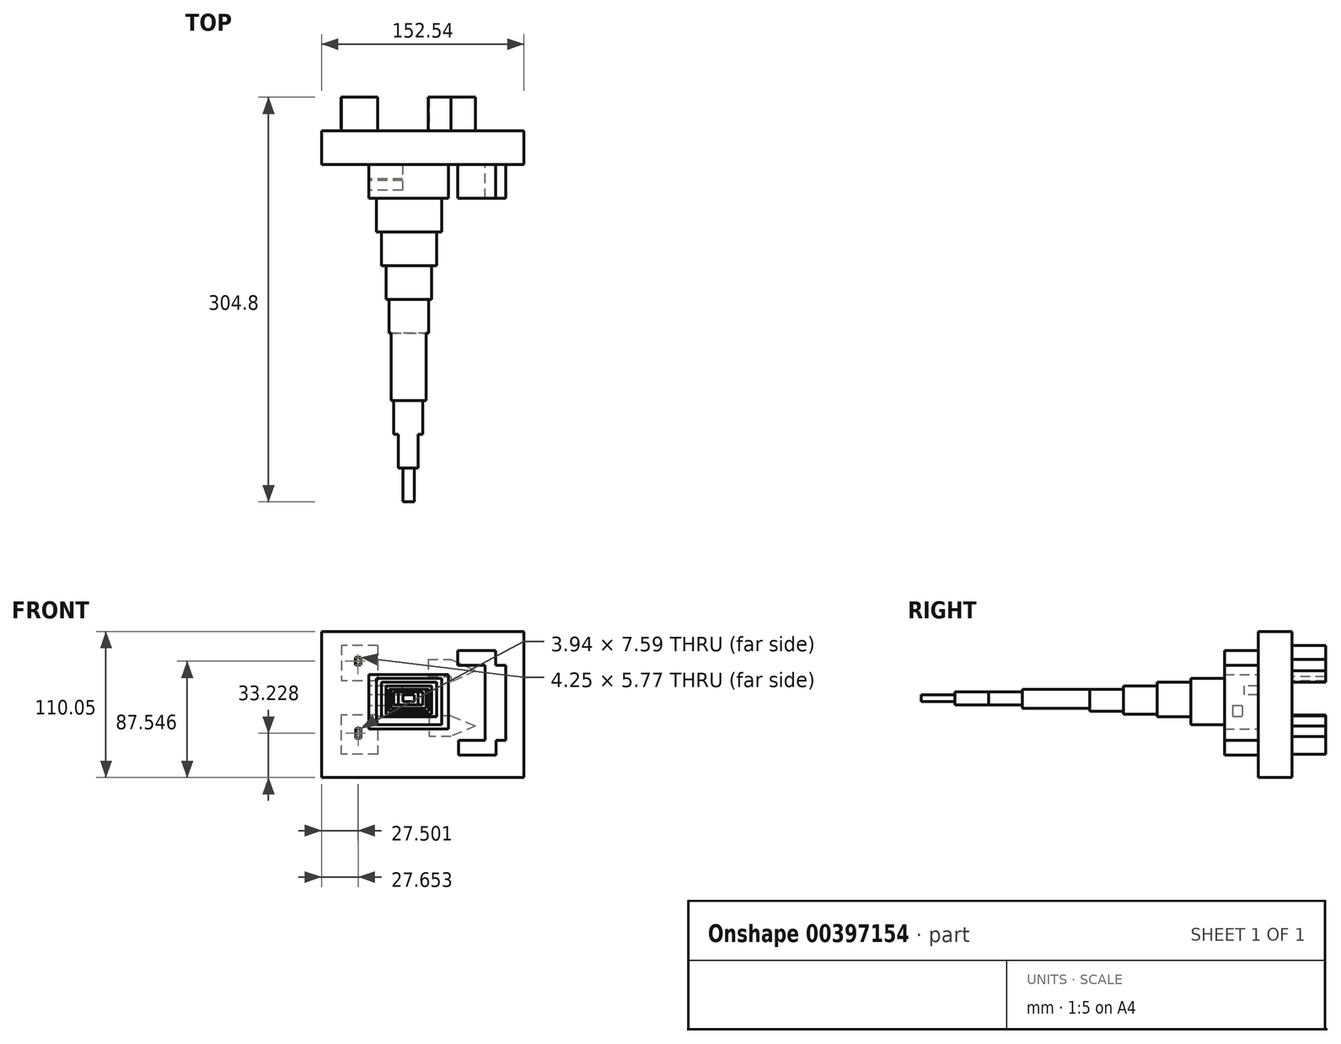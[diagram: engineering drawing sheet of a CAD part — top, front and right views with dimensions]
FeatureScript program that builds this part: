
annotation { "Feature Type Name" : "Feature", "Feature Type Description" : "" }
export const myFeature = defineFeature(function(context is Context, id is Id, definition is map)
    precondition{}
    {
        {
            var Q0;
            Q0=qCreatedBy(makeId("Front.planeOp"),FACE);
            var sketch = newSketch(context, id + "F0", { "sketchPlane" : qUnion([Q0])});
            skLineSegment(sketch, "E0.bottom", {"start": v(-76.07, 75.76) * mm, "end": v(76.47, 75.76) * mm});
            skLineSegment(sketch, "E0.top", {"start": v(-76.07, -34.3) * mm, "end": v(76.47, -34.3) * mm});
            skLineSegment(sketch, "E0.left", {"start": v(-76.07, 75.76) * mm, "end": v(-76.07, -34.3) * mm});
            skLineSegment(sketch, "E0.right", {"start": v(76.47, 75.76) * mm, "end": v(76.47, -34.3) * mm});
            skSolve(sketch);
        }
        {
            var Q0;
            Q0 = qSketchRegion(id + "F0", true);
            extrude(context, id + "F1", {"entities" : qUnion([Q0]), "depth" : 25.4 * mm});
        }
        {
            var Q0;
            Q0=makeQuery(id+"F1.opExtrude","CAP_FACE",FACE,{"disambiguationData":[OSD([sQuery(id+"F0.wireOp",EDGE,"E0.bottom"),sQuery(id+"F0.wireOp",EDGE,"E0.top"),sQuery(id+"F0.wireOp",EDGE,"E0.left"),sQuery(id+"F0.wireOp",EDGE,"E0.right")])],"isStart":false});
            var sketch = newSketch(context, id + "F2", { "sketchPlane" : qUnion([Q0])});
            skLineSegment(sketch, "E1.bottom", {"start": v(19.56, 2.12) * mm, "end": v(-40.33, 2.12) * mm});
            skLineSegment(sketch, "E1.top", {"start": v(19.56, 43.2) * mm, "end": v(-40.33, 43.2) * mm});
            skLineSegment(sketch, "E1.left", {"start": v(19.56, 2.12) * mm, "end": v(19.56, 43.2) * mm});
            skLineSegment(sketch, "E1.right", {"start": v(-40.33, 2.12) * mm, "end": v(-40.33, 43.2) * mm});
            skSolve(sketch);
        }
        {
            var Q0;
            Q0=makeQuery(id+"F2.imprint","IMPRINT",FACE,{"disambiguationData":[TD([[makeQuery(id+"F2.imprint","IMPRINT",EDGE,{"derivedFrom":sQuery(id+"F2.wireOp",EDGE,"E1.bottom")}),-1.0]])]});
            extrude(context, id + "F3", {"entities" : qUnion([Q0]), "operationType" : NewBodyOperationType.ADD, "depth" : 25.4 * mm});
        }
        {
            var Q0;
            Q0=makeQuery(id+"F3.opExtrude","SWEPT_FACE",FACE,{"disambiguationData":[OSD([sQuery(id+"F2.wireOp",EDGE,"E1.right")])]});
            var sketch = newSketch(context, id + "F4", { "sketchPlane" : qUnion([Q0])});
            skLineSegment(sketch, "E2.bottom", {"start": v(25.4, 34.8) * mm, "end": v(35.98, 34.8) * mm});
            skLineSegment(sketch, "E2.top", {"start": v(25.4, 28.12) * mm, "end": v(35.98, 28.12) * mm});
            skLineSegment(sketch, "E2.left", {"start": v(25.4, 34.8) * mm, "end": v(25.4, 28.12) * mm});
            skLineSegment(sketch, "E2.right", {"start": v(35.98, 34.8) * mm, "end": v(35.98, 28.12) * mm});
            skPoint(sketch, "E3.firstSnap0", {"position": v(30.69, 28.12) * mm});
            skLineSegment(sketch, "E3.bottom", {"start": v(30.69, 29.94) * mm, "end": v(30.69, 29.94) * mm});
            skLineSegment(sketch, "E3.top", {"start": v(30.69, 28.12) * mm, "end": v(30.69, 28.12) * mm});
            skLineSegment(sketch, "E3.left", {"start": v(30.69, 29.94) * mm, "end": v(30.69, 28.12) * mm});
            skLineSegment(sketch, "E3.right", {"start": v(30.69, 29.94) * mm, "end": v(30.69, 28.12) * mm});
            skSolve(sketch);
        }
        {
            var Q0;
            Q0=makeQuery(id+"F4.imprint","IMPRINT",FACE,{"disambiguationData":[TD([[makeQuery(id+"F4.imprint","IMPRINT",EDGE,{"derivedFrom":sQuery(id+"F4.wireOp",EDGE,"E2.bottom")}),-1.0]])]});
            extrude(context, id + "F5", {"entities" : qUnion([Q0]), "operationType" : NewBodyOperationType.REMOVE, "oppositeDirection" : true, "depth" : 25.4 * mm});
        }
        {
            var Q0;
            Q0=makeQuery(id+"F3.opExtrude","SWEPT_FACE",FACE,{"disambiguationData":[OSD([sQuery(id+"F2.wireOp",EDGE,"E1.right")])]});
            var sketch = newSketch(context, id + "F6", { "sketchPlane" : qUnion([Q0])});
            skLineSegment(sketch, "E4.bottom", {"start": v(37.44, 19.62) * mm, "end": v(44.52, 19.62) * mm});
            skLineSegment(sketch, "E4.top", {"start": v(37.44, 11.53) * mm, "end": v(44.52, 11.53) * mm});
            skLineSegment(sketch, "E4.left", {"start": v(37.44, 19.62) * mm, "end": v(37.44, 11.53) * mm});
            skLineSegment(sketch, "E4.right", {"start": v(44.52, 19.62) * mm, "end": v(44.52, 11.53) * mm});
            skLineSegment(sketch, "E5.bottom", {"start": v(37.44, 15.58) * mm, "end": v(44.52, 15.58) * mm});
            skLineSegment(sketch, "E5.top", {"start": v(37.44, 15.58) * mm, "end": v(44.52, 15.58) * mm});
            skLineSegment(sketch, "E5.left", {"start": v(37.44, 15.58) * mm, "end": v(37.44, 15.58) * mm});
            skLineSegment(sketch, "E5.right", {"start": v(44.52, 15.58) * mm, "end": v(44.52, 15.58) * mm});
            skLineSegment(sketch, "E6.bottom", {"start": v(40.98, 19.62) * mm, "end": v(40.98, 19.62) * mm});
            skLineSegment(sketch, "E6.top", {"start": v(40.98, 11.53) * mm, "end": v(40.98, 11.53) * mm});
            skLineSegment(sketch, "E6.left", {"start": v(40.98, 19.62) * mm, "end": v(40.98, 11.53) * mm});
            skLineSegment(sketch, "E6.right", {"start": v(40.98, 19.62) * mm, "end": v(40.98, 11.53) * mm});
            skSolve(sketch);
        }
        {
            var Q0;
            {var subQ0=sQuery(id+"F6.wireOp",EDGE,"E4.left");var subQ1=sQuery(id+"F6.wireOp",EDGE,"E4.bottom");var subQ2=makeQuery(id+"F6.imprint","INTERSECT",VERTEX,{"derivedFrom":[subQ1,subQ0]});Q0=makeQuery(id+"F6.imprint","IMPRINT",FACE,{"disambiguationData":[TD([[makeQuery(id+"F6.imprint","IMPRINT",EDGE,{"disambiguationData":[TD([[subQ2,-1.0]])],"derivedFrom":subQ1}),-1.0]])]});}
            var Q1;
            {var subQ0=sQuery(id+"F6.wireOp",EDGE,"E4.left");var subQ1=sQuery(id+"F6.wireOp",EDGE,"E4.top");var subQ2=makeQuery(id+"F6.imprint","INTERSECT",VERTEX,{"derivedFrom":[subQ1,subQ0]});Q1=makeQuery(id+"F6.imprint","IMPRINT",FACE,{"disambiguationData":[TD([[makeQuery(id+"F6.imprint","IMPRINT",EDGE,{"disambiguationData":[TD([[subQ2,-1.0]])],"derivedFrom":subQ1}),1.0]])]});}
            var Q2;
            {var subQ0=sQuery(id+"F6.wireOp",EDGE,"E4.right");var subQ1=sQuery(id+"F6.wireOp",EDGE,"E4.top");var subQ2=makeQuery(id+"F6.imprint","INTERSECT",VERTEX,{"derivedFrom":[subQ1,subQ0]});Q2=makeQuery(id+"F6.imprint","IMPRINT",FACE,{"disambiguationData":[TD([[makeQuery(id+"F6.imprint","IMPRINT",EDGE,{"disambiguationData":[TD([[subQ2,1.0]])],"derivedFrom":subQ1}),1.0]])]});}
            var Q3;
            {var subQ0=sQuery(id+"F6.wireOp",EDGE,"E4.right");var subQ1=sQuery(id+"F6.wireOp",EDGE,"E4.bottom");var subQ2=makeQuery(id+"F6.imprint","INTERSECT",VERTEX,{"derivedFrom":[subQ1,subQ0]});Q3=makeQuery(id+"F6.imprint","IMPRINT",FACE,{"disambiguationData":[TD([[makeQuery(id+"F6.imprint","IMPRINT",EDGE,{"disambiguationData":[TD([[subQ2,1.0]])],"derivedFrom":subQ1}),-1.0]])]});}
            extrude(context, id + "F7", {"entities" : qUnion([Q0, Q1, Q2, Q3]), "operationType" : NewBodyOperationType.REMOVE, "oppositeDirection" : true, "depth" : 25.4 * mm});
        }
        {
            var Q0;
            Q0=makeQuery(id+"F3.opExtrude","CAP_FACE",FACE,{"disambiguationData":[OSD([sQuery(id+"F2.wireOp",EDGE,"E1.bottom"),sQuery(id+"F2.wireOp",EDGE,"E1.top"),sQuery(id+"F2.wireOp",EDGE,"E1.left"),sQuery(id+"F2.wireOp",EDGE,"E1.right")])],"isStart":false});
            var sketch = newSketch(context, id + "F8", { "sketchPlane" : qUnion([Q0])});
            skLineSegment(sketch, "E7.bottom", {"start": v(-34.8, 40.3) * mm, "end": v(14.6, 40.3) * mm});
            skLineSegment(sketch, "E7.top", {"start": v(-34.8, 5.6) * mm, "end": v(14.6, 5.6) * mm});
            skLineSegment(sketch, "E7.left", {"start": v(-34.8, 40.3) * mm, "end": v(-34.8, 5.6) * mm});
            skLineSegment(sketch, "E7.right", {"start": v(14.6, 40.3) * mm, "end": v(14.6, 5.6) * mm});
            skSolve(sketch);
        }
        {
            var Q0;
            Q0=makeQuery(id+"F8.imprint","IMPRINT",FACE,{"disambiguationData":[TD([[makeQuery(id+"F8.imprint","IMPRINT",EDGE,{"derivedFrom":sQuery(id+"F8.wireOp",EDGE,"E7.bottom")}),-1.0]])]});
            extrude(context, id + "F9", {"entities" : qUnion([Q0]), "operationType" : NewBodyOperationType.ADD, "depth" : 25.4 * mm});
        }
        {
            var Q0;
            Q0=makeQuery(id+"F9.opExtrude","CAP_FACE",FACE,{"disambiguationData":[OSD([sQuery(id+"F8.wireOp",EDGE,"E7.bottom"),sQuery(id+"F8.wireOp",EDGE,"E7.top"),sQuery(id+"F8.wireOp",EDGE,"E7.left"),sQuery(id+"F8.wireOp",EDGE,"E7.right")])],"isStart":false});
            var sketch = newSketch(context, id + "F10", { "sketchPlane" : qUnion([Q0])});
            skLineSegment(sketch, "E8.bottom", {"start": v(-31.01, 11.5) * mm, "end": v(10.66, 11.5) * mm});
            skLineSegment(sketch, "E8.top", {"start": v(-31.01, 37.43) * mm, "end": v(10.66, 37.43) * mm});
            skLineSegment(sketch, "E8.left", {"start": v(-31.01, 11.5) * mm, "end": v(-31.01, 37.43) * mm});
            skLineSegment(sketch, "E8.right", {"start": v(10.66, 11.5) * mm, "end": v(10.66, 37.43) * mm});
            skSolve(sketch);
        }
        {
            var Q0;
            Q0=makeQuery(id+"F10.imprint","IMPRINT",FACE,{"disambiguationData":[TD([[makeQuery(id+"F10.imprint","IMPRINT",EDGE,{"derivedFrom":sQuery(id+"F10.wireOp",EDGE,"E8.bottom")}),1.0]])]});
            extrude(context, id + "F11", {"entities" : qUnion([Q0]), "operationType" : NewBodyOperationType.ADD, "depth" : 25.4 * mm});
        }
        {
            var Q0;
            Q0=makeQuery(id+"F11.opExtrude","CAP_FACE",FACE,{"disambiguationData":[OSD([sQuery(id+"F10.wireOp",EDGE,"E8.bottom"),sQuery(id+"F10.wireOp",EDGE,"E8.top"),sQuery(id+"F10.wireOp",EDGE,"E8.left"),sQuery(id+"F10.wireOp",EDGE,"E8.right")])],"isStart":false});
            var sketch = newSketch(context, id + "F12", { "sketchPlane" : qUnion([Q0])});
            skLineSegment(sketch, "E9.bottom", {"start": v(-27.32, 34.5) * mm, "end": v(6.74, 34.5) * mm});
            skLineSegment(sketch, "E9.top", {"start": v(-27.32, 13.3) * mm, "end": v(6.74, 13.3) * mm});
            skLineSegment(sketch, "E9.left", {"start": v(-27.32, 34.5) * mm, "end": v(-27.32, 13.3) * mm});
            skLineSegment(sketch, "E9.right", {"start": v(6.74, 34.5) * mm, "end": v(6.74, 13.3) * mm});
            skSolve(sketch);
        }
        {
            var Q0;
            Q0=makeQuery(id+"F12.imprint","IMPRINT",FACE,{"disambiguationData":[TD([[makeQuery(id+"F12.imprint","IMPRINT",EDGE,{"derivedFrom":sQuery(id+"F12.wireOp",EDGE,"E9.bottom")}),-1.0]])]});
            extrude(context, id + "F13", {"entities" : qUnion([Q0]), "operationType" : NewBodyOperationType.ADD, "depth" : 25.4 * mm});
        }
        {
            var Q0;
            Q0=makeQuery(id+"F13.opExtrude","CAP_FACE",FACE,{"disambiguationData":[OSD([sQuery(id+"F12.wireOp",EDGE,"E9.bottom"),sQuery(id+"F12.wireOp",EDGE,"E9.top"),sQuery(id+"F12.wireOp",EDGE,"E9.left"),sQuery(id+"F12.wireOp",EDGE,"E9.right")])],"isStart":false});
            var sketch = newSketch(context, id + "F14", { "sketchPlane" : qUnion([Q0])});
            skLineSegment(sketch, "E10.bottom", {"start": v(4.59, 32.27) * mm, "end": v(-25.15, 32.27) * mm});
            skLineSegment(sketch, "E10.top", {"start": v(4.59, 15.48) * mm, "end": v(-25.15, 15.48) * mm});
            skLineSegment(sketch, "E10.left", {"start": v(4.59, 32.27) * mm, "end": v(4.59, 15.48) * mm});
            skLineSegment(sketch, "E10.right", {"start": v(-25.15, 32.27) * mm, "end": v(-25.15, 15.48) * mm});
            skSolve(sketch);
        }
        {
            var Q0;
            Q0=makeQuery(id+"F14.imprint","IMPRINT",FACE,{"disambiguationData":[TD([[makeQuery(id+"F14.imprint","IMPRINT",EDGE,{"derivedFrom":sQuery(id+"F14.wireOp",EDGE,"E10.bottom")}),1.0]])]});
            extrude(context, id + "F15", {"entities" : qUnion([Q0]), "operationType" : NewBodyOperationType.ADD, "depth" : 25.4 * mm});
        }
        {
            var Q0;
            Q0=makeQuery(id+"F15.opExtrude","CAP_FACE",FACE,{"disambiguationData":[OSD([sQuery(id+"F14.wireOp",EDGE,"E10.bottom"),sQuery(id+"F14.wireOp",EDGE,"E10.top"),sQuery(id+"F14.wireOp",EDGE,"E10.left"),sQuery(id+"F14.wireOp",EDGE,"E10.right")])],"isStart":false});
            var sketch = newSketch(context, id + "F16", { "sketchPlane" : qUnion([Q0])});
            skLineSegment(sketch, "E11.bottom", {"start": v(-23.53, 17.9) * mm, "end": v(2.76, 17.9) * mm});
            skLineSegment(sketch, "E11.top", {"start": v(-23.53, 32.27) * mm, "end": v(2.76, 32.27) * mm});
            skLineSegment(sketch, "E11.left", {"start": v(-23.53, 17.9) * mm, "end": v(-23.53, 32.27) * mm});
            skLineSegment(sketch, "E11.right", {"start": v(2.76, 17.9) * mm, "end": v(2.76, 32.27) * mm});
            skLineSegment(sketch, "E12.bottom", {"start": v(-22.12, 20.33) * mm, "end": v(0.74, 20.33) * mm});
            skLineSegment(sketch, "E12.top", {"start": v(-22.12, 30.65) * mm, "end": v(0.74, 30.65) * mm});
            skLineSegment(sketch, "E12.left", {"start": v(-22.12, 20.33) * mm, "end": v(-22.12, 30.65) * mm});
            skLineSegment(sketch, "E12.right", {"start": v(0.74, 20.33) * mm, "end": v(0.74, 30.65) * mm});
            skSolve(sketch);
        }
        {
            var Q0;
            Q0=makeQuery(id+"F16.imprint","IMPRINT",FACE,{"disambiguationData":[TD([[makeQuery(id+"F16.imprint","IMPRINT",EDGE,{"derivedFrom":sQuery(id+"F16.wireOp",EDGE,"E11.bottom")}),1.0]])]});
            var Q1;
            Q1=makeQuery(id+"F16.imprint","IMPRINT",FACE,{"disambiguationData":[TD([[makeQuery(id+"F16.imprint","IMPRINT",EDGE,{"derivedFrom":sQuery(id+"F16.wireOp",EDGE,"E12.bottom")}),1.0]])]});
            extrude(context, id + "F17", {"entities" : qUnion([Q0, Q1]), "operationType" : NewBodyOperationType.ADD, "depth" : 25.4 * mm});
        }
        {
            var Q0;
            Q0=makeQuery(id+"F17.opExtrude","CAP_FACE",FACE,{"disambiguationData":[OSD([sQuery(id+"F16.wireOp",EDGE,"E11.bottom"),sQuery(id+"F16.wireOp",EDGE,"E11.top"),sQuery(id+"F16.wireOp",EDGE,"E11.left"),sQuery(id+"F16.wireOp",EDGE,"E11.right")])],"isStart":false});
            var sketch = newSketch(context, id + "F18", { "sketchPlane" : qUnion([Q0])});
            skLineSegment(sketch, "E13.bottom", {"start": v(-22.12, 20.33) * mm, "end": v(0.34, 20.33) * mm});
            skLineSegment(sketch, "E13.top", {"start": v(-22.12, 30.45) * mm, "end": v(0.34, 30.45) * mm});
            skLineSegment(sketch, "E13.left", {"start": v(-22.12, 20.33) * mm, "end": v(-22.12, 30.45) * mm});
            skLineSegment(sketch, "E13.right", {"start": v(0.34, 20.33) * mm, "end": v(0.34, 30.45) * mm});
            skLineSegment(sketch, "E14.bottom", {"start": v(-20.5, 22.35) * mm, "end": v(-2.1, 22.35) * mm});
            skLineSegment(sketch, "E14.top", {"start": v(-20.5, 28.83) * mm, "end": v(-2.1, 28.83) * mm});
            skLineSegment(sketch, "E14.left", {"start": v(-20.5, 22.35) * mm, "end": v(-20.5, 28.83) * mm});
            skLineSegment(sketch, "E14.right", {"start": v(-2.1, 22.35) * mm, "end": v(-2.1, 28.83) * mm});
            skLineSegment(sketch, "E15.bottom", {"start": v(-18.68, 24.17) * mm, "end": v(-4.32, 24.17) * mm});
            skLineSegment(sketch, "E15.top", {"start": v(-18.68, 28.83) * mm, "end": v(-4.32, 28.83) * mm});
            skLineSegment(sketch, "E15.left", {"start": v(-18.68, 24.17) * mm, "end": v(-18.68, 28.83) * mm});
            skLineSegment(sketch, "E15.right", {"start": v(-4.32, 24.17) * mm, "end": v(-4.32, 28.83) * mm});
            skLineSegment(sketch, "E16.bottom", {"start": v(-16.45, 25.8) * mm, "end": v(-7.96, 25.8) * mm});
            skLineSegment(sketch, "E16.top", {"start": v(-16.45, 27.2) * mm, "end": v(-7.96, 27.2) * mm});
            skLineSegment(sketch, "E16.left", {"start": v(-16.45, 25.8) * mm, "end": v(-16.45, 27.2) * mm});
            skLineSegment(sketch, "E16.right", {"start": v(-7.96, 25.8) * mm, "end": v(-7.96, 27.2) * mm});
            skSolve(sketch);
        }
        {
            var Q0;
            Q0=makeQuery(id+"F18.imprint","IMPRINT",FACE,{"disambiguationData":[TD([[makeQuery(id+"F18.imprint","IMPRINT",EDGE,{"derivedFrom":sQuery(id+"F18.wireOp",EDGE,"E13.bottom")}),-1.0]])]});
            var Q1;
            Q1=makeQuery(id+"F18.imprint","IMPRINT",FACE,{"disambiguationData":[TD([[makeQuery(id+"F18.imprint","IMPRINT",EDGE,{"derivedFrom":sQuery(id+"F18.wireOp",EDGE,"E13.bottom")}),1.0]])]});
            var Q2;
            Q2=makeQuery(id+"F18.imprint","IMPRINT",FACE,{"disambiguationData":[TD([[makeQuery(id+"F18.imprint","IMPRINT",EDGE,{"derivedFrom":sQuery(id+"F18.wireOp",EDGE,"E14.bottom")}),1.0]])]});
            var Q3;
            Q3=makeQuery(id+"F18.imprint","IMPRINT",FACE,{"disambiguationData":[TD([[makeQuery(id+"F18.imprint","IMPRINT",EDGE,{"derivedFrom":sQuery(id+"F18.wireOp",EDGE,"E15.bottom")}),1.0]])]});
            var Q4;
            Q4=makeQuery(id+"F18.imprint","IMPRINT",FACE,{"disambiguationData":[TD([[makeQuery(id+"F18.imprint","IMPRINT",EDGE,{"derivedFrom":sQuery(id+"F18.wireOp",EDGE,"E16.bottom")}),1.0]])]});
            extrude(context, id + "F19", {"entities" : qUnion([Q0, Q1, Q2, Q3, Q4]), "operationType" : NewBodyOperationType.ADD, "depth" : 25.4 * mm});
        }
        {
            var Q0;
            Q0=makeQuery(id+"F19.opExtrude","CAP_FACE",FACE,{"disambiguationData":[OSD([sQuery(id+"F16.wireOp",EDGE,"E11.bottom"),sQuery(id+"F16.wireOp",EDGE,"E11.top"),sQuery(id+"F16.wireOp",EDGE,"E11.left"),sQuery(id+"F16.wireOp",EDGE,"E11.right")])],"isStart":false});
            var sketch = newSketch(context, id + "F20", { "sketchPlane" : qUnion([Q0])});
            skLineSegment(sketch, "E17.bottom", {"start": v(-21.71, 20.33) * mm, "end": v(0.13, 20.33) * mm});
            skLineSegment(sketch, "E17.top", {"start": v(-21.71, 30.24) * mm, "end": v(0.13, 30.24) * mm});
            skLineSegment(sketch, "E17.left", {"start": v(-21.71, 20.33) * mm, "end": v(-21.71, 30.24) * mm});
            skLineSegment(sketch, "E17.right", {"start": v(0.13, 20.33) * mm, "end": v(0.13, 30.24) * mm});
            skSolve(sketch);
        }
        {
            var Q0;
            Q0=makeQuery(id+"F20.imprint","IMPRINT",FACE,{"disambiguationData":[TD([[makeQuery(id+"F20.imprint","IMPRINT",EDGE,{"derivedFrom":sQuery(id+"F20.wireOp",EDGE,"E17.bottom")}),1.0]])]});
            extrude(context, id + "F21", {"entities" : qUnion([Q0]), "operationType" : NewBodyOperationType.ADD, "depth" : 25.4 * mm});
        }
        {
            var Q0;
            Q0=makeQuery(id+"F21.opExtrude","CAP_FACE",FACE,{"disambiguationData":[OSD([sQuery(id+"F20.wireOp",EDGE,"E17.bottom"),sQuery(id+"F20.wireOp",EDGE,"E17.top"),sQuery(id+"F20.wireOp",EDGE,"E17.left"),sQuery(id+"F20.wireOp",EDGE,"E17.right")])],"isStart":false});
            var sketch = newSketch(context, id + "F22", { "sketchPlane" : qUnion([Q0])});
            skLineSegment(sketch, "E18.bottom", {"start": v(-18.22, 30.24) * mm, "end": v(-3.35, 30.24) * mm});
            skLineSegment(sketch, "E18.top", {"start": v(-18.22, 20.33) * mm, "end": v(-3.35, 20.33) * mm});
            skLineSegment(sketch, "E18.left", {"start": v(-18.22, 30.24) * mm, "end": v(-18.22, 20.33) * mm});
            skLineSegment(sketch, "E18.right", {"start": v(-3.35, 30.24) * mm, "end": v(-3.35, 20.33) * mm});
            skSolve(sketch);
        }
        {
            var Q0;
            Q0=makeQuery(id+"F22.imprint","IMPRINT",FACE,{"disambiguationData":[TD([[makeQuery(id+"F22.imprint","IMPRINT",EDGE,{"derivedFrom":sQuery(id+"F22.wireOp",EDGE,"E18.bottom")}),-1.0]])]});
            extrude(context, id + "F23", {"entities" : qUnion([Q0]), "operationType" : NewBodyOperationType.ADD, "depth" : 25.4 * mm});
        }
        {
            var Q0;
            Q0=makeQuery(id+"F23.opExtrude","CAP_FACE",FACE,{"disambiguationData":[OSD([sQuery(id+"F22.wireOp",EDGE,"E18.bottom"),sQuery(id+"F22.wireOp",EDGE,"E18.top"),sQuery(id+"F22.wireOp",EDGE,"E18.left"),sQuery(id+"F22.wireOp",EDGE,"E18.right")])],"isStart":false});
            var sketch = newSketch(context, id + "F24", { "sketchPlane" : qUnion([Q0])});
            skLineSegment(sketch, "E19.bottom", {"start": v(-14.89, 27.92) * mm, "end": v(-6.09, 27.92) * mm});
            skLineSegment(sketch, "E19.top", {"start": v(-14.89, 23.06) * mm, "end": v(-6.09, 23.06) * mm});
            skLineSegment(sketch, "E19.left", {"start": v(-14.89, 27.92) * mm, "end": v(-14.89, 23.06) * mm});
            skLineSegment(sketch, "E19.right", {"start": v(-6.09, 27.92) * mm, "end": v(-6.09, 23.06) * mm});
            skSolve(sketch);
        }
        {
            var Q0;
            Q0=makeQuery(id+"F24.imprint","IMPRINT",FACE,{"disambiguationData":[TD([[makeQuery(id+"F24.imprint","IMPRINT",EDGE,{"derivedFrom":sQuery(id+"F24.wireOp",EDGE,"E19.bottom")}),-1.0]])]});
            extrude(context, id + "F25", {"entities" : qUnion([Q0]), "operationType" : NewBodyOperationType.ADD, "depth" : 25.4 * mm});
        }
        {
            var Q0;
            Q0=makeQuery(id+"F1.opExtrude","CAP_FACE",FACE,{"disambiguationData":[OSD([sQuery(id+"F0.wireOp",EDGE,"E0.bottom"),sQuery(id+"F0.wireOp",EDGE,"E0.top"),sQuery(id+"F0.wireOp",EDGE,"E0.left"),sQuery(id+"F0.wireOp",EDGE,"E0.right")])],"isStart":true});
            var sketch = newSketch(context, id + "F26", { "sketchPlane" : qUnion([Q0])});
            skLineSegment(sketch, "E20.bottom", {"start": v(33.7, 65.24) * mm, "end": v(61.01, 65.24) * mm});
            skLineSegment(sketch, "E20.top", {"start": v(33.7, 38.54) * mm, "end": v(61.01, 38.54) * mm});
            skLineSegment(sketch, "E20.left", {"start": v(33.7, 65.24) * mm, "end": v(33.7, 38.54) * mm});
            skLineSegment(sketch, "E20.right", {"start": v(61.01, 65.24) * mm, "end": v(61.01, 38.54) * mm});
            skLineSegment(sketch, "E21.bottom", {"start": v(42.5, 58.87) * mm, "end": v(53.73, 58.87) * mm});
            skLineSegment(sketch, "E21.top", {"start": v(42.5, 47.34) * mm, "end": v(53.73, 47.34) * mm});
            skLineSegment(sketch, "E21.left", {"start": v(42.5, 58.87) * mm, "end": v(42.5, 47.34) * mm});
            skLineSegment(sketch, "E21.right", {"start": v(53.73, 58.87) * mm, "end": v(53.73, 47.34) * mm});
            skLineSegment(sketch, "E22.bottom", {"start": v(46.44, 56.14) * mm, "end": v(50.7, 56.14) * mm});
            skLineSegment(sketch, "E22.top", {"start": v(46.44, 50.37) * mm, "end": v(50.7, 50.37) * mm});
            skLineSegment(sketch, "E22.left", {"start": v(46.44, 56.14) * mm, "end": v(46.44, 50.37) * mm});
            skLineSegment(sketch, "E22.right", {"start": v(50.7, 56.14) * mm, "end": v(50.7, 50.37) * mm});
            skLineSegment(sketch, "E23.bottom", {"start": v(33.7, 12.74) * mm, "end": v(61.31, 12.74) * mm});
            skLineSegment(sketch, "E23.top", {"start": v(33.7, -16.69) * mm, "end": v(61.31, -16.69) * mm});
            skLineSegment(sketch, "E23.left", {"start": v(33.7, 12.74) * mm, "end": v(33.7, -16.69) * mm});
            skLineSegment(sketch, "E23.right", {"start": v(61.31, 12.74) * mm, "end": v(61.31, -16.69) * mm});
            skLineSegment(sketch, "E24.bottom", {"start": v(43.1, 6.37) * mm, "end": v(52.82, 6.37) * mm});
            skLineSegment(sketch, "E24.top", {"start": v(43.1, -8.8) * mm, "end": v(52.82, -8.8) * mm});
            skLineSegment(sketch, "E24.left", {"start": v(43.1, 6.37) * mm, "end": v(43.1, -8.8) * mm});
            skLineSegment(sketch, "E24.right", {"start": v(52.82, 6.37) * mm, "end": v(52.82, -8.8) * mm});
            skLineSegment(sketch, "E25.bottom", {"start": v(46.44, 2.73) * mm, "end": v(50.39, 2.73) * mm});
            skLineSegment(sketch, "E25.top", {"start": v(46.44, -4.86) * mm, "end": v(50.39, -4.86) * mm});
            skLineSegment(sketch, "E25.left", {"start": v(46.44, 2.73) * mm, "end": v(46.44, -4.86) * mm});
            skLineSegment(sketch, "E25.right", {"start": v(50.39, 2.73) * mm, "end": v(50.39, -4.86) * mm});
            skLineSegment(sketch, "E26.bottom", {"start": v(-4.23, 54.62) * mm, "end": v(-21.53, 54.62) * mm});
            skLineSegment(sketch, "E26.top", {"start": v(-4.23, 41.57) * mm, "end": v(-21.53, 41.57) * mm});
            skLineSegment(sketch, "E26.left", {"start": v(-4.23, 54.62) * mm, "end": v(-4.23, 41.57) * mm});
            skLineSegment(sketch, "E26.right", {"start": v(-21.53, 54.62) * mm, "end": v(-21.53, 41.57) * mm});
            skLineSegment(sketch, "E27.bottom", {"start": v(-12.88, 41.57) * mm, "end": v(-21.53, 41.57) * mm});
            skLineSegment(sketch, "E27.top", {"start": v(-12.88, 12.14) * mm, "end": v(-21.53, 12.14) * mm});
            skLineSegment(sketch, "E27.left", {"start": v(-12.88, 41.57) * mm, "end": v(-12.88, 12.14) * mm});
            skLineSegment(sketch, "E27.right", {"start": v(-21.53, 41.57) * mm, "end": v(-21.53, 12.14) * mm});
            skLineSegment(sketch, "E28.bottom", {"start": v(-21.53, 12.14) * mm, "end": v(-4.84, 12.14) * mm});
            skLineSegment(sketch, "E28.top", {"start": v(-21.53, -3.34) * mm, "end": v(-4.84, -3.34) * mm});
            skLineSegment(sketch, "E28.left", {"start": v(-21.53, 12.14) * mm, "end": v(-21.53, -3.34) * mm});
            skLineSegment(sketch, "E28.right", {"start": v(-4.84, 12.14) * mm, "end": v(-4.84, -3.34) * mm});
            skLineSegment(sketch, "E29", {"start": v(-21.53, 54.62) * mm, "end": v(-40.04, 46.12) * mm});
            skLineSegment(sketch, "E30", {"start": v(-40.04, 46.12) * mm, "end": v(-21.53, 37.63) * mm});
            skLineSegment(sketch, "E31", {"start": v(-21.53, 12.14) * mm, "end": v(-40.04, 4.55) * mm});
            skLineSegment(sketch, "E32", {"start": v(-40.04, 4.55) * mm, "end": v(-21.53, -3.34) * mm});
            skSolve(sketch);
        }
        {
            var Q0;
            Q0=makeQuery(id+"F26.imprint","IMPRINT",FACE,{"disambiguationData":[TD([[makeQuery(id+"F26.imprint","IMPRINT",EDGE,{"derivedFrom":sQuery(id+"F26.wireOp",EDGE,"E21.bottom")}),-1.0]])]});
            var Q1;
            Q1=makeQuery(id+"F26.imprint","IMPRINT",FACE,{"disambiguationData":[TD([[makeQuery(id+"F26.imprint","IMPRINT",EDGE,{"derivedFrom":sQuery(id+"F26.wireOp",EDGE,"E20.bottom")}),-1.0]])]});
            var Q2;
            Q2=makeQuery(id+"F26.imprint","IMPRINT",FACE,{"disambiguationData":[TD([[makeQuery(id+"F26.imprint","IMPRINT",EDGE,{"derivedFrom":sQuery(id+"F26.wireOp",EDGE,"E23.bottom")}),-1.0]])]});
            var Q3;
            Q3=makeQuery(id+"F26.imprint","IMPRINT",FACE,{"disambiguationData":[TD([[makeQuery(id+"F26.imprint","IMPRINT",EDGE,{"derivedFrom":sQuery(id+"F26.wireOp",EDGE,"E24.bottom")}),-1.0]])]});
            var Q4;
            Q4=makeQuery(id+"F26.imprint","IMPRINT",FACE,{"disambiguationData":[TD([[makeQuery(id+"F26.imprint","IMPRINT",EDGE,{"derivedFrom":sQuery(id+"F26.wireOp",EDGE,"E26.bottom")}),1.0]])]});
            var Q5;
            {var subQ4=sQuery(id+"F26.wireOp",EDGE,"E27.bottom");Q5=makeQuery(id+"F26.imprint","IMPRINT",FACE,{"disambiguationData":[TD([[makeQuery(id+"F26.imprint","IMPRINT",EDGE,{"derivedFrom":subQ4}),1.0]])]});}
            var Q6;
            Q6=makeQuery(id+"F26.imprint","IMPRINT",FACE,{"disambiguationData":[TD([[makeQuery(id+"F26.imprint","IMPRINT",EDGE,{"derivedFrom":sQuery(id+"F26.wireOp",EDGE,"E28.top")}),1.0]])]});
            var Q7;
            Q7=makeQuery(id+"F26.imprint","IMPRINT",FACE,{"disambiguationData":[TD([[makeQuery(id+"F26.imprint","IMPRINT",EDGE,{"derivedFrom":sQuery(id+"F26.wireOp",EDGE,"E28.left")}),-1.0]])]});
            var Q8;
            {var subQ0=sQuery(id+"F26.wireOp",EDGE,"E26.right");Q8=makeQuery(id+"F26.imprint","IMPRINT",FACE,{"disambiguationData":[TD([[makeQuery(id+"F26.imprint","IMPRINT",EDGE,{"derivedFrom":subQ0}),-1.0]])]});}
            extrude(context, id + "F27", {"entities" : qUnion([Q0, Q1, Q2, Q3, Q4, Q5, Q6, Q7, Q8]), "operationType" : NewBodyOperationType.ADD, "depth" : 25.4 * mm});
        }
        {
            var Q0;
            Q0=makeQuery(id+"F27.boolean.opBoolean","SPLIT",FACE,{"disambiguationData":[TD([makeQuery(id+"F27.opExtrude","SWEPT_FACE",FACE,{"disambiguationData":[OSD([sQuery(id+"F26.wireOp",EDGE,"E22.bottom")])]})])],"derivedFrom":makeQuery(id+"F1.opExtrude","CAP_FACE",FACE,{"disambiguationData":[OSD([sQuery(id+"F0.wireOp",EDGE,"E0.bottom"),sQuery(id+"F0.wireOp",EDGE,"E0.top"),sQuery(id+"F0.wireOp",EDGE,"E0.left"),sQuery(id+"F0.wireOp",EDGE,"E0.right")])],"isStart":true})});
            var Q1;
            Q1=makeQuery(id+"F27.boolean.opBoolean","SPLIT",FACE,{"disambiguationData":[TD([makeQuery(id+"F27.opExtrude","SWEPT_FACE",FACE,{"disambiguationData":[OSD([sQuery(id+"F26.wireOp",EDGE,"E25.bottom")])]})])],"derivedFrom":makeQuery(id+"F1.opExtrude","CAP_FACE",FACE,{"disambiguationData":[OSD([sQuery(id+"F0.wireOp",EDGE,"E0.bottom"),sQuery(id+"F0.wireOp",EDGE,"E0.top"),sQuery(id+"F0.wireOp",EDGE,"E0.left"),sQuery(id+"F0.wireOp",EDGE,"E0.right")])],"isStart":true})});
            extrude(context, id + "F28", {"entities" : qUnion([Q0, Q1]), "operationType" : NewBodyOperationType.REMOVE, "oppositeDirection" : true, "depth" : 25.4 * mm});
        }
        {
            var Q0;
            Q0=makeQuery(id+"F5.boolean.opBoolean","MERGE",FACE,{"derivedFrom":[makeQuery(id+"F1.opExtrude","CAP_FACE",FACE,{"disambiguationData":[OSD([sQuery(id+"F0.wireOp",EDGE,"E0.bottom"),sQuery(id+"F0.wireOp",EDGE,"E0.top"),sQuery(id+"F0.wireOp",EDGE,"E0.left"),sQuery(id+"F0.wireOp",EDGE,"E0.right")])],"isStart":false}),makeQuery(id+"F5.opExtrude","SWEPT_FACE",FACE,{"disambiguationData":[OSD([sQuery(id+"F4.wireOp",EDGE,"E2.left")])]})]});
            var sketch = newSketch(context, id + "F29", { "sketchPlane" : qUnion([Q0])});
            skLineSegment(sketch, "E33.bottom", {"start": v(27.04, -6.17) * mm, "end": v(55.57, -6.17) * mm});
            skLineSegment(sketch, "E33.top", {"start": v(27.04, -17.5) * mm, "end": v(55.57, -17.5) * mm});
            skLineSegment(sketch, "E33.left", {"start": v(27.04, -6.17) * mm, "end": v(27.04, -17.5) * mm});
            skLineSegment(sketch, "E33.right", {"start": v(55.57, -6.17) * mm, "end": v(55.57, -17.5) * mm});
            skLineSegment(sketch, "E34.bottom", {"start": v(47.27, -6.17) * mm, "end": v(62.85, -6.17) * mm});
            skLineSegment(sketch, "E34.top", {"start": v(47.27, 50.27) * mm, "end": v(62.85, 50.27) * mm});
            skLineSegment(sketch, "E34.left", {"start": v(47.27, -6.17) * mm, "end": v(47.27, 50.27) * mm});
            skLineSegment(sketch, "E34.right", {"start": v(62.85, -6.17) * mm, "end": v(62.85, 50.27) * mm});
            skLineSegment(sketch, "E35.bottom", {"start": v(55.06, 50.27) * mm, "end": v(26.43, 50.27) * mm});
            skLineSegment(sketch, "E35.top", {"start": v(55.06, 61.4) * mm, "end": v(26.43, 61.4) * mm});
            skLineSegment(sketch, "E35.left", {"start": v(55.06, 50.27) * mm, "end": v(55.06, 61.4) * mm});
            skLineSegment(sketch, "E35.right", {"start": v(26.43, 50.27) * mm, "end": v(26.43, 61.4) * mm});
            skSolve(sketch);
        }
        {
            var Q0;
            Q0=makeQuery(id+"F29.imprint","IMPRINT",FACE,{"disambiguationData":[TD([[makeQuery(id+"F29.imprint","IMPRINT",EDGE,{"derivedFrom":sQuery(id+"F29.wireOp",EDGE,"E35.top")}),1.0]])]});
            var Q1;
            {var subQ1=sQuery(id+"F29.wireOp",EDGE,"E34.top");Q1=makeQuery(id+"F29.imprint","IMPRINT",FACE,{"disambiguationData":[TD([[makeQuery(id+"F29.imprint","IMPRINT",EDGE,{"derivedFrom":subQ1}),-1.0]])]});}
            var Q2;
            {var subQ1=sQuery(id+"F29.wireOp",EDGE,"E33.bottom");Q2=makeQuery(id+"F29.imprint","IMPRINT",FACE,{"disambiguationData":[TD([[makeQuery(id+"F29.imprint","IMPRINT",EDGE,{"derivedFrom":subQ1}),-1.0]])]});}
            extrude(context, id + "F30", {"entities" : qUnion([Q0, Q1, Q2]), "operationType" : NewBodyOperationType.ADD, "depth" : 25.4 * mm});
        }
    });
